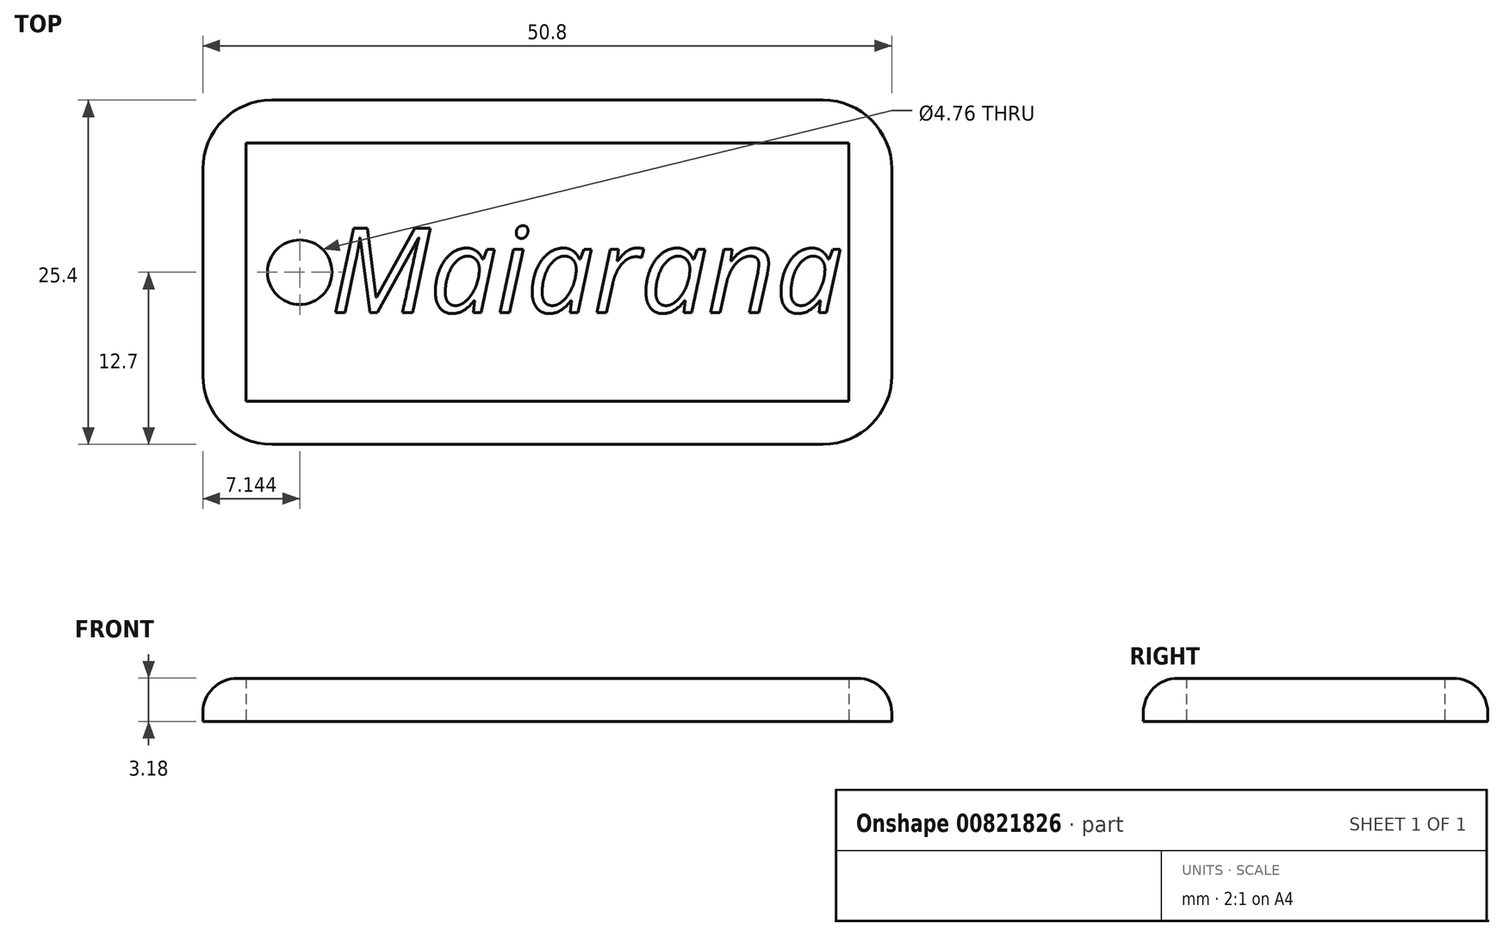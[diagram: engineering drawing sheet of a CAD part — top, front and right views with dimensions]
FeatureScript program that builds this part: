
annotation { "Feature Type Name" : "Feature", "Feature Type Description" : "" }
export const myFeature = defineFeature(function(context is Context, id is Id, definition is map)
    precondition{}
    {
        {
            var Q0;
            Q0=qCreatedBy(makeId("Top.planeOp"),FACE);
            var sketch = newSketch(context, id + "F0", { "sketchPlane" : qUnion([Q0])});
            skLineSegment(sketch, "E0.bottom", {"start": v(0, 0) * mm, "end": v(50.8, 0) * mm});
            skLineSegment(sketch, "E0.top", {"start": v(0, 25.4) * mm, "end": v(50.8, 25.4) * mm});
            skLineSegment(sketch, "E0.left", {"start": v(0, 0) * mm, "end": v(0, 25.4) * mm});
            skLineSegment(sketch, "E0.right", {"start": v(50.8, 0) * mm, "end": v(50.8, 25.4) * mm});
            skCircle(sketch, "E1", {"center": v(7.14, 12.7) * mm, "radius": 2.38 * mm});
            skPoint(sketch, "E1.centerSnap0", {"position": v(0, 12.7) * mm});
            skLineSegment(sketch, "E2.0", {"start": v(3.17, 22.22) * mm, "end": v(47.62, 22.22) * mm});
            skLineSegment(sketch, "E2.1", {"start": v(3.18, 3.18) * mm, "end": v(3.17, 22.22) * mm});
            skLineSegment(sketch, "E2.2", {"start": v(3.18, 3.18) * mm, "end": v(47.62, 3.18) * mm});
            skLineSegment(sketch, "E2.3", {"start": v(47.62, 3.18) * mm, "end": v(47.62, 22.23) * mm});
            skSolve(sketch);
        }
        {
            var Q0;
            Q0=makeQuery(id+"F0.imprint","IMPRINT",FACE,{"disambiguationData":[TD([[makeQuery(id+"F0.imprint","IMPRINT",EDGE,{"derivedFrom":sQuery(id+"F0.wireOp",EDGE,"E1")}),-1.0]])]});
            extrude(context, id + "F1", {"entities" : qUnion([Q0]), "depth" : 1 / 406.4 * mm, "offsetDistance" : 25.4 * mm});
        }
        {
            var Q0;
            Q0 = qSketchRegion(id + "F0", true);
            extrude(context, id + "F2", {"entities" : qUnion([Q0]), "operationType" : NewBodyOperationType.ADD, "depth" : 3.17 * mm, "offsetDistance" : 25.4 * mm});
        }
        {
            var Q0;
            Q0=makeQuery(id+"F2.opExtrude","SWEPT_EDGE",EDGE,{"disambiguationData":[OSD([sQuery(id+"F0.wireOp",EDGE,"E0.bottom"),sQuery(id+"F0.wireOp",EDGE,"E0.right")])]});
            var Q1;
            Q1=makeQuery(id+"F2.opExtrude","SWEPT_EDGE",EDGE,{"disambiguationData":[OSD([sQuery(id+"F0.wireOp",EDGE,"E0.bottom"),sQuery(id+"F0.wireOp",EDGE,"E0.left")])]});
            var Q2;
            Q2=makeQuery(id+"F2.opExtrude","SWEPT_EDGE",EDGE,{"disambiguationData":[OSD([sQuery(id+"F0.wireOp",EDGE,"E0.top"),sQuery(id+"F0.wireOp",EDGE,"E0.right")])]});
            var Q3;
            Q3=makeQuery(id+"F2.opExtrude","SWEPT_EDGE",EDGE,{"disambiguationData":[OSD([sQuery(id+"F0.wireOp",EDGE,"E0.top"),sQuery(id+"F0.wireOp",EDGE,"E0.left")])]});
            fillet(context, id + "F3", {"entities" : qUnion([Q0, Q1, Q2, Q3]), "radius" : 5.08 * mm, "tangentPropagation" : true, "allowEdgeOverflow" : false});
        }
        {
            var Q0;
            Q0=makeQuery(id+"F2.opExtrude","CAP_EDGE",EDGE,{"disambiguationData":[OSD([sQuery(id+"F0.wireOp",EDGE,"E0.top")])],"isStart":false});
            var Q1;
            Q1=makeQuery(id+"F2.opExtrude","CAP_EDGE",EDGE,{"disambiguationData":[OSD([sQuery(id+"F0.wireOp",EDGE,"E0.bottom")])],"isStart":false});
            fillet(context, id + "F4", {"entities" : qUnion([Q0, Q1]), "radius" : 2.54 * mm, "tangentPropagation" : true, "allowEdgeOverflow" : false});
        }
        {
            var Q0;
            Q0=makeQuery(id+"F1.opExtrude","CAP_FACE",FACE,{"disambiguationData":[OSD([sQuery(id+"F0.wireOp",EDGE,"E1"),sQuery(id+"F0.wireOp",EDGE,"E2.0"),sQuery(id+"F0.wireOp",EDGE,"E2.1"),sQuery(id+"F0.wireOp",EDGE,"E2.2"),sQuery(id+"F0.wireOp",EDGE,"E2.3")])],"isStart":false});
            var sketch = newSketch(context, id + "F5", { "sketchPlane" : qUnion([Q0])});
            skText(sketch, "E3", { "text": "Maiarana", "fontName": "OpenSans-Italic.ttf"});
            const initialGuessF5  = {"E3": [0.00943, 0.00973, 1, 0, 0.00628]};
            skSetInitialGuess(sketch, initialGuessF5);
            skSolve(sketch);
        }
        {
            var Q0;
            Q0 = qSketchRegion(id + "F5", true);
            extrude(context, id + "F6", {"entities" : qUnion([Q0]), "operationType" : NewBodyOperationType.ADD, "depth" : 1 / 812.8 * mm, "offsetDistance" : 25.4 * mm});
        }
    });
